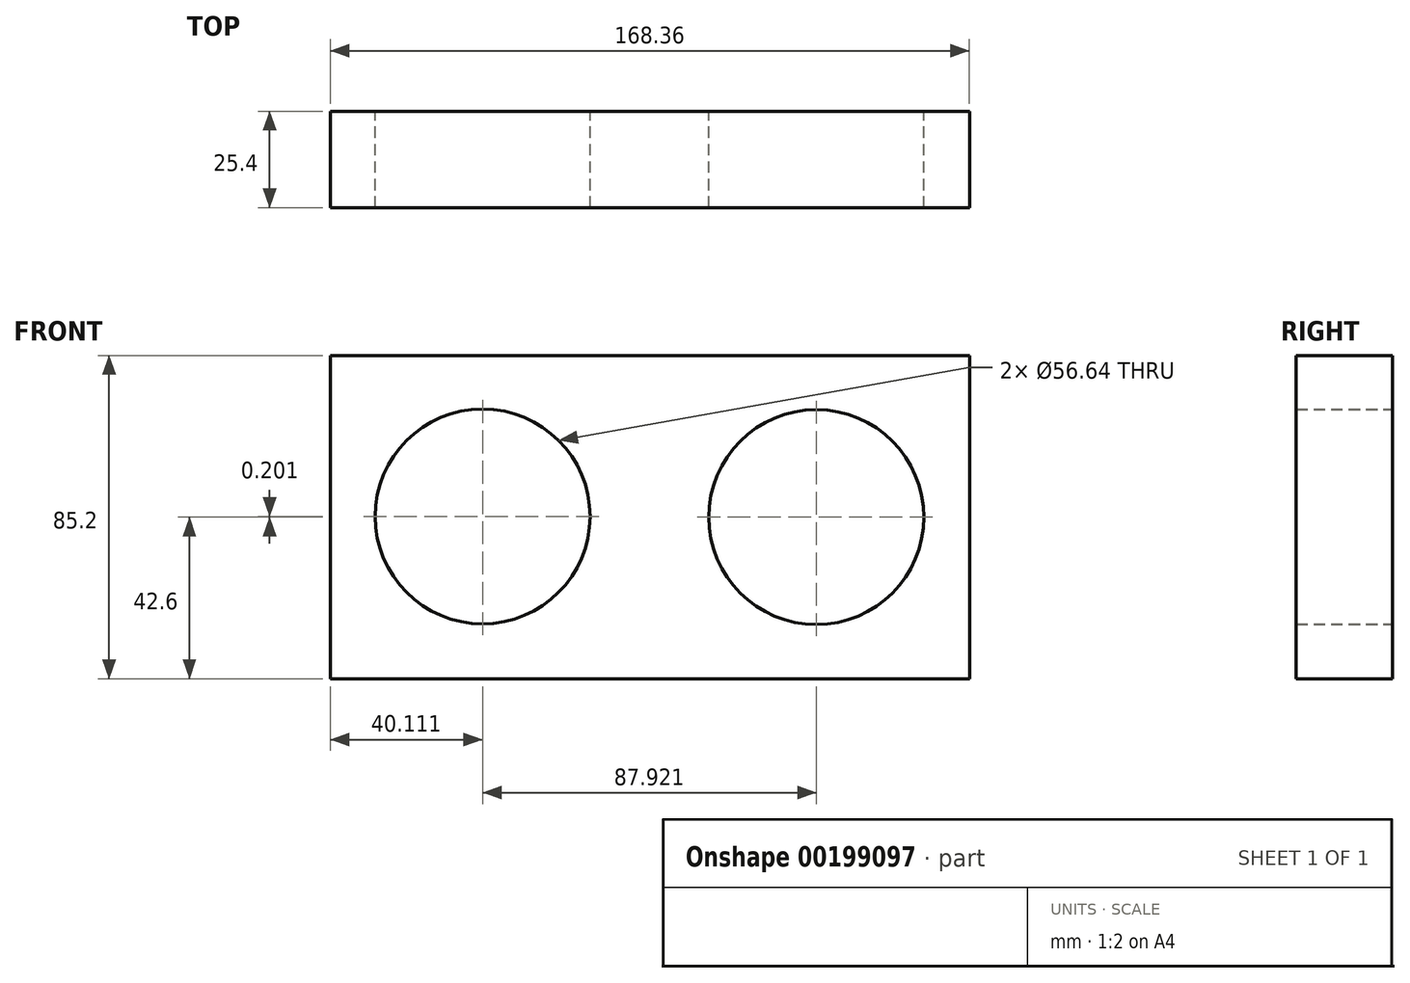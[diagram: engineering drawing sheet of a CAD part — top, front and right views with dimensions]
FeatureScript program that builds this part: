
annotation { "Feature Type Name" : "Feature", "Feature Type Description" : "" }
export const myFeature = defineFeature(function(context is Context, id is Id, definition is map)
    precondition{}
    {
        {
            var Q0;
            Q0=qCreatedBy(makeId("Front.planeOp"),FACE);
            var sketch = newSketch(context, id + "F0", { "sketchPlane" : qUnion([Q0])});
            skLineSegment(sketch, "E0.bottom", {"start": v(84.18, -42.6) * mm, "end": v(-84.18, -42.6) * mm});
            skLineSegment(sketch, "E0.top", {"start": v(84.18, 42.6) * mm, "end": v(-84.18, 42.6) * mm});
            skLineSegment(sketch, "E0.left", {"start": v(84.18, -42.6) * mm, "end": v(84.18, 42.6) * mm});
            skLineSegment(sketch, "E0.right", {"start": v(-84.18, -42.6) * mm, "end": v(-84.18, 42.6) * mm});
            skPoint(sketch, "E0.middle", {"position": v(0, 0) * mm});
            skCircle(sketch, "E1", {"center": v(43.85, 0) * mm, "radius": 28.32 * mm});
            skCircle(sketch, "E2", {"center": v(-44.07, 0.2) * mm, "radius": 28.32 * mm});
            skSolve(sketch);
        }
        {
            var Q0;
            Q0=makeQuery(id+"F0.imprint","IMPRINT",FACE,{"disambiguationData":[TD([[makeQuery(id+"F0.imprint","IMPRINT",EDGE,{"derivedFrom":sQuery(id+"F0.wireOp",EDGE,"E0.bottom")}),-1.0]])]});
            extrude(context, id + "F1", {"entities" : qUnion([Q0]), "depth" : 25.4 * mm});
        }
    });
